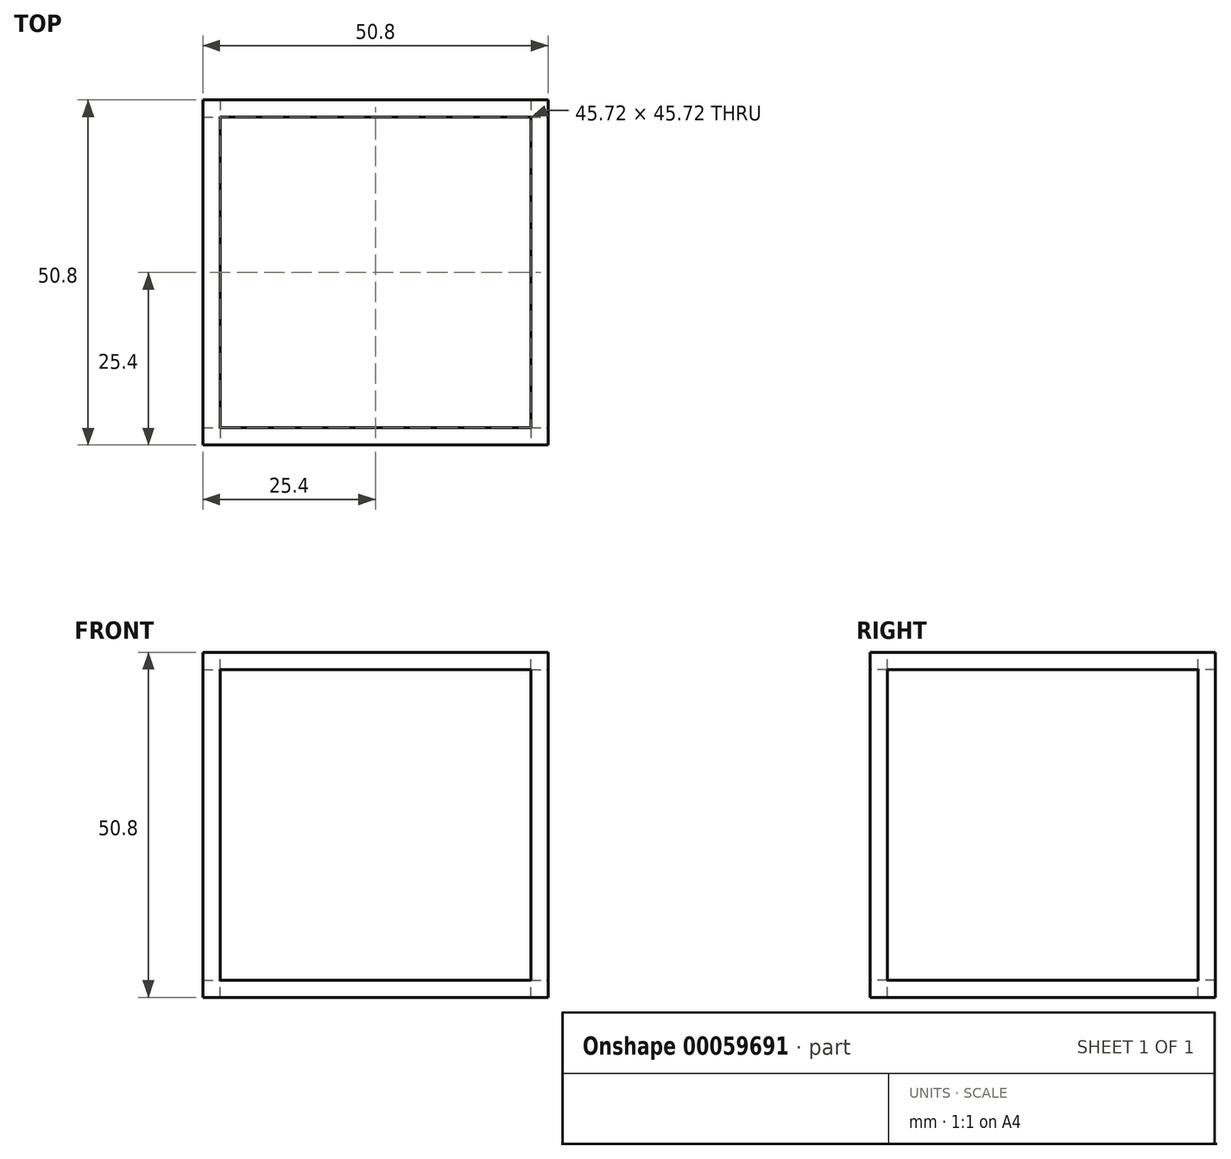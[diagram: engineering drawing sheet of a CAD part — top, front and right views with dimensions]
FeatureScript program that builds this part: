
annotation { "Feature Type Name" : "Feature", "Feature Type Description" : "" }
export const myFeature = defineFeature(function(context is Context, id is Id, definition is map)
    precondition{}
    {
        {
            var Q0;
            Q0=qCreatedBy(makeId("Top.planeOp"),FACE);
            var sketch = newSketch(context, id + "F0", { "sketchPlane" : qUnion([Q0])});
            skLineSegment(sketch, "E0.bottom", {"start": v(0, 0) * mm, "end": v(50.8, 0) * mm});
            skLineSegment(sketch, "E0.top", {"start": v(0, -50.8) * mm, "end": v(50.8, -50.8) * mm});
            skLineSegment(sketch, "E0.left", {"start": v(0, 0) * mm, "end": v(0, -50.8) * mm});
            skLineSegment(sketch, "E0.right", {"start": v(50.8, 0) * mm, "end": v(50.8, -50.8) * mm});
            skSolve(sketch);
        }
        {
            var Q0;
            Q0 = qSketchRegion(id + "F0", true);
            extrude(context, id + "F1", {"entities" : qUnion([Q0]), "depth" : 50.8 * mm});
        }
        {
            var Q0;
            Q0=makeQuery(id+"F1.opExtrude","CAP_FACE",FACE,{"disambiguationData":[OSD([sQuery(id+"F0.wireOp",EDGE,"E0.bottom"),sQuery(id+"F0.wireOp",EDGE,"E0.top"),sQuery(id+"F0.wireOp",EDGE,"E0.left"),sQuery(id+"F0.wireOp",EDGE,"E0.right")])],"isStart":false});
            var sketch = newSketch(context, id + "F2", { "sketchPlane" : qUnion([Q0])});
            skLineSegment(sketch, "E1.bottom", {"start": v(2.54, -2.54) * mm, "end": v(48.26, -2.54) * mm});
            skLineSegment(sketch, "E1.top", {"start": v(2.54, -48.26) * mm, "end": v(48.26, -48.26) * mm});
            skLineSegment(sketch, "E1.left", {"start": v(2.54, -2.54) * mm, "end": v(2.54, -48.26) * mm});
            skLineSegment(sketch, "E1.right", {"start": v(48.26, -2.54) * mm, "end": v(48.26, -48.26) * mm});
            skSolve(sketch);
        }
        {
            var Q0;
            Q0 = qSketchRegion(id + "F2", true);
            extrude(context, id + "F3", {"entities" : qUnion([Q0]), "operationType" : NewBodyOperationType.REMOVE, "oppositeDirection" : true, "depth" : 50.8 * mm});
        }
        {
            var Q0;
            Q0=makeQuery(id+"F1.opExtrude","SWEPT_FACE",FACE,{"disambiguationData":[OSD([sQuery(id+"F0.wireOp",EDGE,"E0.top")])]});
            var sketch = newSketch(context, id + "F4", { "sketchPlane" : qUnion([Q0])});
            skLineSegment(sketch, "E2.bottom", {"start": v(2.54, 48.26) * mm, "end": v(48.26, 48.26) * mm});
            skLineSegment(sketch, "E2.top", {"start": v(2.54, 2.54) * mm, "end": v(48.26, 2.54) * mm});
            skLineSegment(sketch, "E2.left", {"start": v(2.54, 48.26) * mm, "end": v(2.54, 2.54) * mm});
            skLineSegment(sketch, "E2.right", {"start": v(48.26, 48.26) * mm, "end": v(48.26, 2.54) * mm});
            skSolve(sketch);
        }
        {
            var Q0;
            Q0 = qSketchRegion(id + "F4", true);
            extrude(context, id + "F5", {"entities" : qUnion([Q0]), "operationType" : NewBodyOperationType.REMOVE, "oppositeDirection" : true, "depth" : 50.8 * mm});
        }
        {
            var Q0;
            Q0=makeQuery(id+"F1.opExtrude","SWEPT_FACE",FACE,{"disambiguationData":[OSD([sQuery(id+"F0.wireOp",EDGE,"E0.right")])]});
            var sketch = newSketch(context, id + "F6", { "sketchPlane" : qUnion([Q0])});
            skLineSegment(sketch, "E3.bottom", {"start": v(-48.26, 48.26) * mm, "end": v(-2.54, 48.26) * mm});
            skLineSegment(sketch, "E3.top", {"start": v(-48.26, 2.54) * mm, "end": v(-2.54, 2.54) * mm});
            skLineSegment(sketch, "E3.left", {"start": v(-48.26, 48.26) * mm, "end": v(-48.26, 2.54) * mm});
            skLineSegment(sketch, "E3.right", {"start": v(-2.54, 48.26) * mm, "end": v(-2.54, 2.54) * mm});
            skSolve(sketch);
        }
        {
            var Q0;
            Q0 = qSketchRegion(id + "F6", true);
            extrude(context, id + "F7", {"entities" : qUnion([Q0]), "operationType" : NewBodyOperationType.REMOVE, "oppositeDirection" : true, "depth" : 50.8 * mm});
        }
    });
